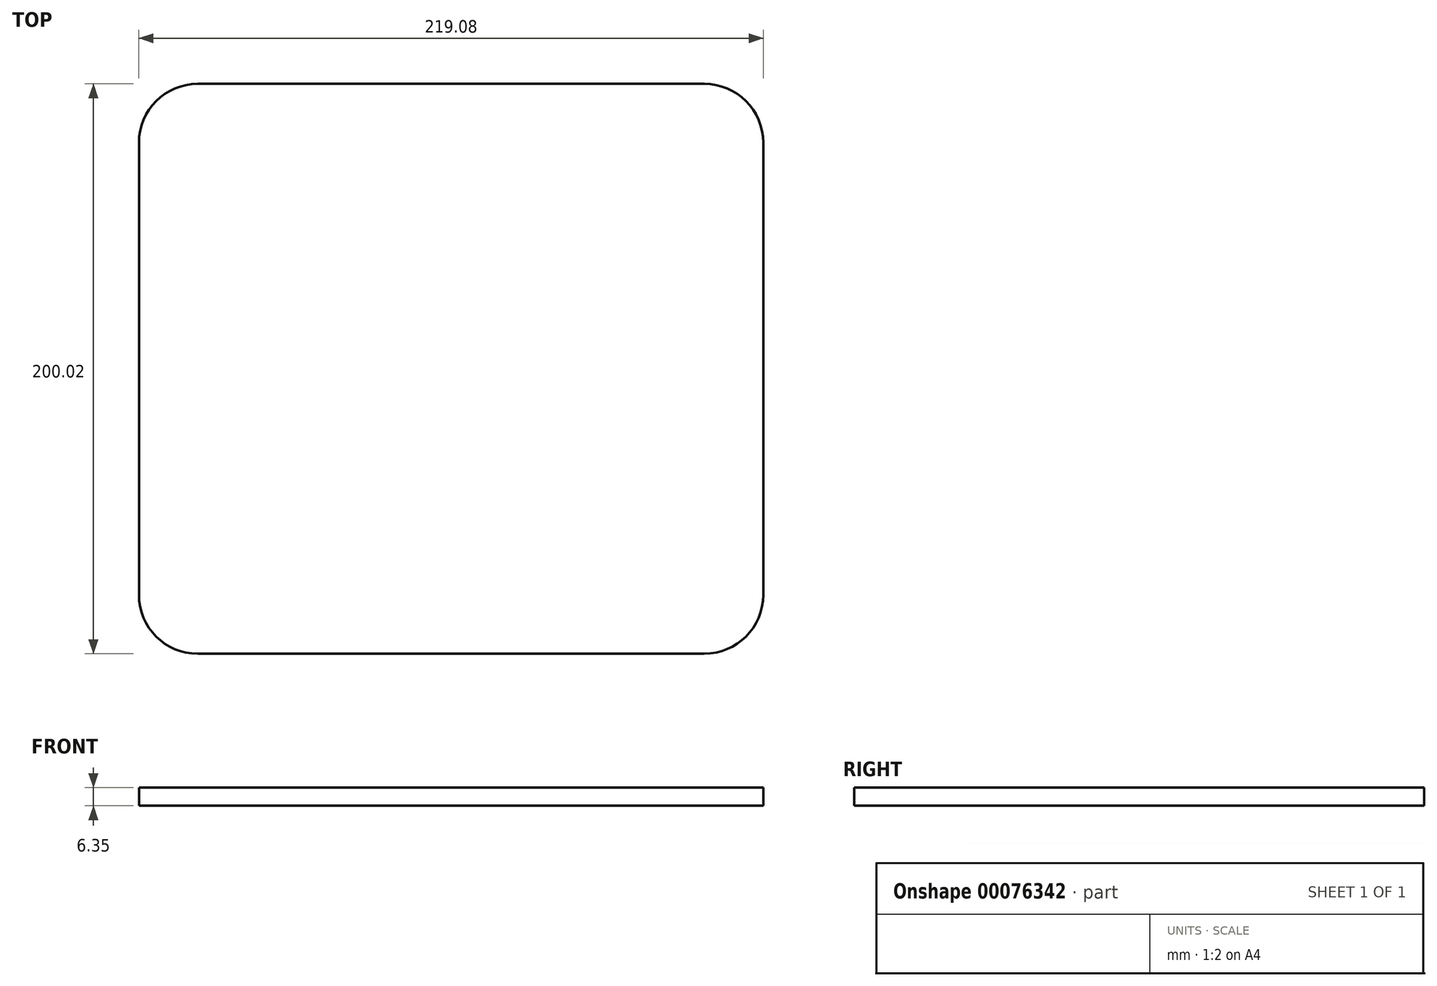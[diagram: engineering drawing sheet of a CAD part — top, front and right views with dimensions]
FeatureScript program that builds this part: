
annotation { "Feature Type Name" : "Feature", "Feature Type Description" : "" }
export const myFeature = defineFeature(function(context is Context, id is Id, definition is map)
    precondition{}
    {
        {
            var Q0;
            Q0=qCreatedBy(makeId("Top.planeOp"),FACE);
            var sketch = newSketch(context, id + "F0", { "sketchPlane" : qUnion([Q0])});
            skLineSegment(sketch, "E0.bottom", {"start": v(-129.1, 126.43) * mm, "end": v(89.97, 126.43) * mm});
            skLineSegment(sketch, "E0.top", {"start": v(-129.1, -73.6) * mm, "end": v(89.97, -73.6) * mm});
            skLineSegment(sketch, "E0.left", {"start": v(-129.1, 126.43) * mm, "end": v(-129.1, -73.6) * mm});
            skLineSegment(sketch, "E0.right", {"start": v(89.97, 126.43) * mm, "end": v(89.97, -73.6) * mm});
            skSolve(sketch);
        }
        {
            var Q0;
            Q0 = qSketchRegion(id + "F0", true);
            extrude(context, id + "F1", {"entities" : qUnion([Q0]), "depth" : 6.35 * mm});
        }
        {
            var Q0;
            Q0=makeQuery(id+"F1.opExtrude","CAP_FACE",FACE,{"disambiguationData":[OSD([sQuery(id+"F0.wireOp",EDGE,"E0.bottom"),sQuery(id+"F0.wireOp",EDGE,"E0.top"),sQuery(id+"F0.wireOp",EDGE,"E0.left"),sQuery(id+"F0.wireOp",EDGE,"E0.right")])],"isStart":false});
            var sketch = newSketch(context, id + "F2", { "sketchPlane" : qUnion([Q0])});
            skLineSegment(sketch, "E1", {"start": v(-129.1, 105.8) * mm, "end": v(-129.1, -52.95) * mm});
            skLineSegment(sketch, "E2", {"start": v(-108.46, 126.43) * mm, "end": v(69.32, 126.43) * mm});
            skLineSegment(sketch, "E3", {"start": v(89.97, 105.78) * mm, "end": v(89.97, -52.94) * mm});
            skLineSegment(sketch, "E4", {"start": v(-108.46, -73.6) * mm, "end": v(69.32, -73.6) * mm});
            skArc(sketch, "E5", {"start": v(-108.46, 126.43) * mm, "mid": v(-123.06, 120.4) * mm, "end": v(-129.1, 105.8) * mm});
            skArc(sketch, "E6", {"start": v(-129.1, -52.95) * mm, "mid": v(-123.06, -67.55) * mm, "end": v(-108.46, -73.6) * mm});
            skArc(sketch, "E7", {"start": v(69.32, -73.6) * mm, "mid": v(83.92, -67.54) * mm, "end": v(89.97, -52.94) * mm});
            skArc(sketch, "E8", {"start": v(89.97, 105.78) * mm, "mid": v(83.92, 120.39) * mm, "end": v(69.32, 126.43) * mm});
            skSolve(sketch);
        }
        {
            var Q0;
            {var subQ0=sQuery(id+"F2.wireOp",EDGE,"E8");Q0=makeQuery(id+"F2.imprint","IMPRINT",FACE,{"disambiguationData":[TD([[makeQuery(id+"F2.imprint","IMPRINT",EDGE,{"derivedFrom":subQ0}),-1.0]])]});}
            var Q1;
            {var subQ0=sQuery(id+"F2.wireOp",EDGE,"E5");Q1=makeQuery(id+"F2.imprint","IMPRINT",FACE,{"disambiguationData":[TD([[makeQuery(id+"F2.imprint","IMPRINT",EDGE,{"derivedFrom":subQ0}),-1.0]])]});}
            var Q2;
            {var subQ0=sQuery(id+"F2.wireOp",EDGE,"E6");Q2=makeQuery(id+"F2.imprint","IMPRINT",FACE,{"disambiguationData":[TD([[makeQuery(id+"F2.imprint","IMPRINT",EDGE,{"derivedFrom":subQ0}),-1.0]])]});}
            var Q3;
            {var subQ0=sQuery(id+"F2.wireOp",EDGE,"E7");Q3=makeQuery(id+"F2.imprint","IMPRINT",FACE,{"disambiguationData":[TD([[makeQuery(id+"F2.imprint","IMPRINT",EDGE,{"derivedFrom":subQ0}),-1.0]])]});}
            extrude(context, id + "F3", {"entities" : qUnion([Q0, Q1, Q2, Q3]), "operationType" : NewBodyOperationType.REMOVE, "endBound" : BoundingType.THROUGH_ALL, "oppositeDirection" : true, "depth" : 25.4 * mm});
        }
    });
